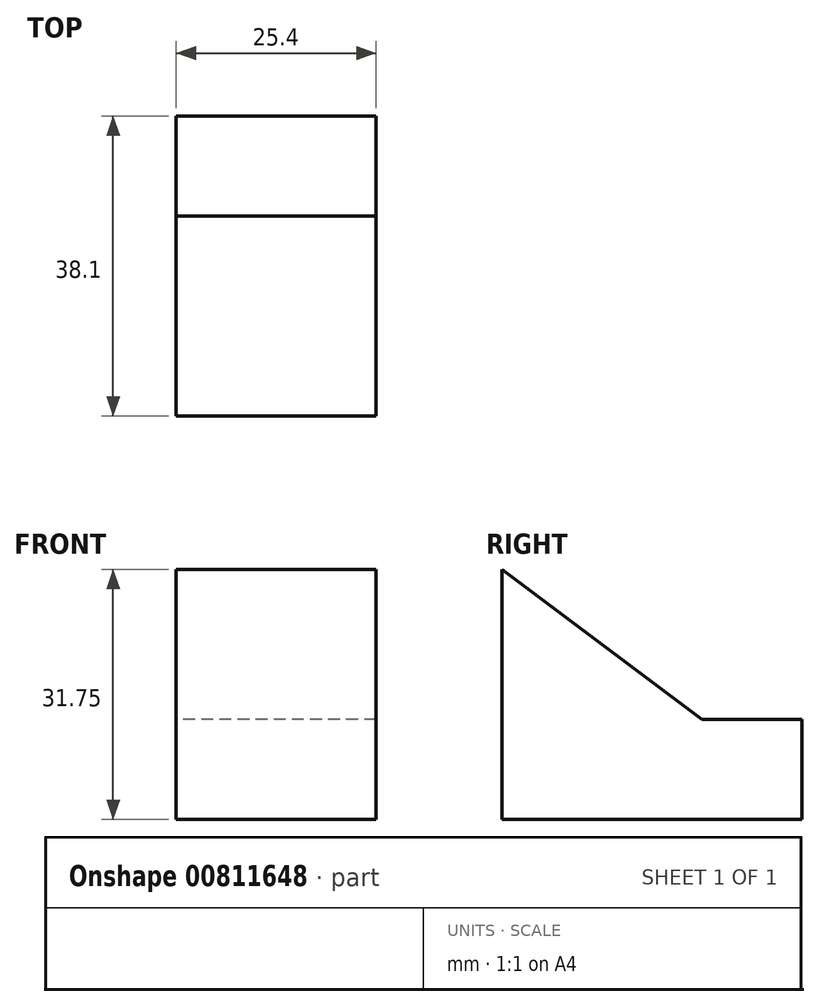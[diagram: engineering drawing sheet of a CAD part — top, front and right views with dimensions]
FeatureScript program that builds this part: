
annotation { "Feature Type Name" : "Feature", "Feature Type Description" : "" }
export const myFeature = defineFeature(function(context is Context, id is Id, definition is map)
    precondition{}
    {
        {
            var Q0;
            Q0=qCreatedBy(makeId("Right.planeOp"),FACE);
            var sketch = newSketch(context, id + "F0", { "sketchPlane" : qUnion([Q0])});
            skLineSegment(sketch, "E0", {"start": v(-12.56, -10.58) * mm, "end": v(-12.56, -42.33) * mm});
            skLineSegment(sketch, "E1", {"start": v(-12.56, -42.33) * mm, "end": v(25.54, -42.33) * mm});
            skLineSegment(sketch, "E2", {"start": v(25.54, -42.33) * mm, "end": v(25.54, -29.63) * mm});
            skLineSegment(sketch, "E3", {"start": v(25.54, -29.63) * mm, "end": v(12.84, -29.63) * mm});
            skLineSegment(sketch, "E4", {"start": v(12.84, -29.63) * mm, "end": v(-12.56, -10.58) * mm});
            skSolve(sketch);
        }
        {
            var Q0;
            Q0=makeQuery(id+"F0.imprint","IMPRINT",FACE,{"disambiguationData":[TD([[makeQuery(id+"F0.imprint","IMPRINT",EDGE,{"derivedFrom":sQuery(id+"F0.wireOp",EDGE,"E0")}),1.0]])]});
            extrude(context, id + "F1", {"entities" : qUnion([Q0]), "depth" : 25.4 * mm, "offsetDistance" : 25.4 * mm});
        }
    });
